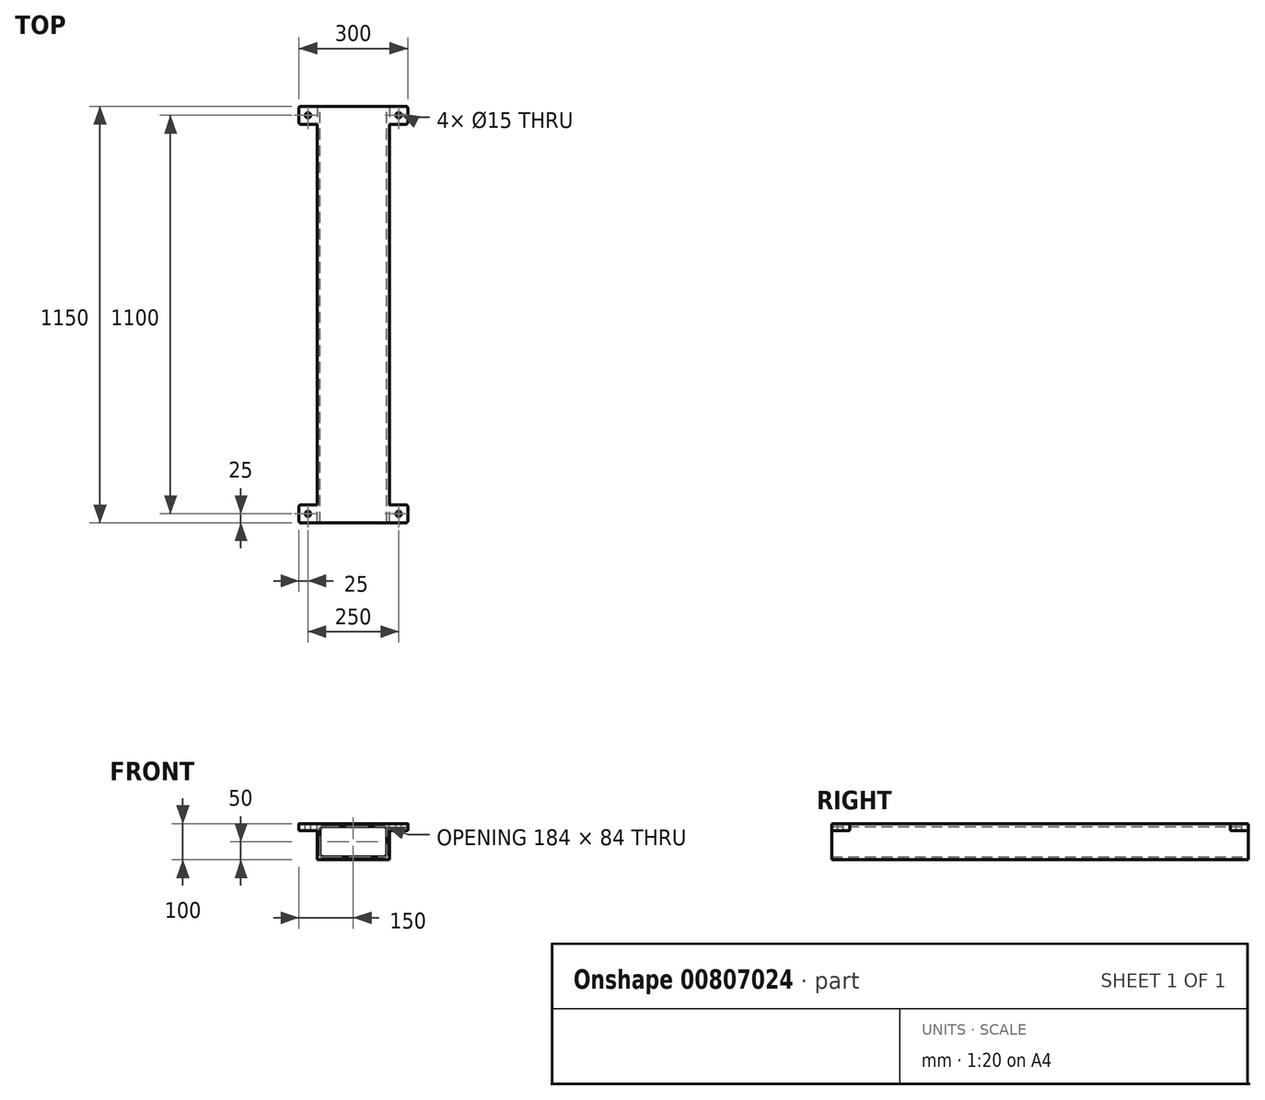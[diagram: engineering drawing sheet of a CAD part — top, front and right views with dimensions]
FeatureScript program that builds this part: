
annotation { "Feature Type Name" : "Feature", "Feature Type Description" : "" }
export const myFeature = defineFeature(function(context is Context, id is Id, definition is map)
    precondition{}
    {
        {
            var Q0;
            Q0=qCreatedBy(makeId("Front.planeOp"),FACE);
            var sketch = newSketch(context, id + "F0", { "sketchPlane" : qUnion([Q0])});
            skLineSegment(sketch, "E0.bottom", {"start": v(-100, 0) * mm, "end": v(100, 0) * mm});
            skLineSegment(sketch, "E0.top", {"start": v(-100, -100) * mm, "end": v(100, -100) * mm});
            skLineSegment(sketch, "E0.left", {"start": v(-100, 0) * mm, "end": v(-100, -100) * mm});
            skLineSegment(sketch, "E0.right", {"start": v(100, 0) * mm, "end": v(100, -100) * mm});
            skLineSegment(sketch, "E1.bottom", {"start": v(-82, -8) * mm, "end": v(82, -8) * mm});
            skLineSegment(sketch, "E1.top", {"start": v(-82, -92) * mm, "end": v(82, -92) * mm});
            skLineSegment(sketch, "E1.left", {"start": v(-92, -18) * mm, "end": v(-92, -82) * mm});
            skLineSegment(sketch, "E1.right", {"start": v(92, -18) * mm, "end": v(92, -82) * mm});
            skPoint(sketch, "E2.visualSharp", {"position": v(-92, -8) * mm});
            skArc(sketch, "E2.filletArc", {"start": v(-82, -8) * mm, "mid": v(-89.07, -10.93) * mm, "end": v(-92, -18) * mm});
            skPoint(sketch, "E3.visualSharp", {"position": v(92, -8) * mm});
            skArc(sketch, "E3.filletArc", {"start": v(92, -18) * mm, "mid": v(89.07, -10.93) * mm, "end": v(82, -8) * mm});
            skPoint(sketch, "E4.visualSharp", {"position": v(92, -92) * mm});
            skArc(sketch, "E4.filletArc", {"start": v(82, -92) * mm, "mid": v(89.07, -89.07) * mm, "end": v(92, -82) * mm});
            skPoint(sketch, "E5.visualSharp", {"position": v(-92, -92) * mm});
            skArc(sketch, "E5.filletArc", {"start": v(-92, -82) * mm, "mid": v(-89.07, -89.07) * mm, "end": v(-82, -92) * mm});
            skLineSegment(sketch, "E6", {"start": v(0, 0) * mm, "end": v(0, -112.71) * mm, "construction": true});
            skSolve(sketch);
        }
        {
            var Q0;
            Q0=makeQuery(id+"F0.imprint","IMPRINT",FACE,{"disambiguationData":[TD([[makeQuery(id+"F0.imprint","IMPRINT",EDGE,{"derivedFrom":sQuery(id+"F0.wireOp",EDGE,"E0.bottom")}),-1.0]])]});
            extrude(context, id + "F1", {"entities" : qUnion([Q0]), "endBound" : BoundingType.SYMMETRIC, "depth" : 1150 * mm, "offsetDistance" : 25 * mm});
        }
        {
            var Q0;
            Q0=makeQuery(id+"F1.opExtrude","SWEPT_FACE",FACE,{"disambiguationData":[OSD([sQuery(id+"F0.wireOp",EDGE,"E0.bottom")])]});
            var sketch = newSketch(context, id + "F2", { "sketchPlane" : qUnion([Q0])});
            skLineSegment(sketch, "E7.bottom", {"start": v(-100, -575) * mm, "end": v(-145, -575) * mm});
            skLineSegment(sketch, "E7.top", {"start": v(-100, -525) * mm, "end": v(-145, -525) * mm});
            skLineSegment(sketch, "E7.left", {"start": v(-100, -575) * mm, "end": v(-100, -525) * mm});
            skLineSegment(sketch, "E7.right", {"start": v(-150, -570) * mm, "end": v(-150, -530) * mm});
            skCircle(sketch, "E8", {"center": v(-125, -550) * mm, "radius": 7.5 * mm});
            skPoint(sketch, "E8.centerSnap0", {"position": v(-125, -525) * mm});
            skPoint(sketch, "E8.centerSnap1", {"position": v(-150, -550) * mm});
            skPoint(sketch, "E9.visualSharp", {"position": v(-150, -525) * mm});
            skArc(sketch, "E9.filletArc", {"start": v(-145, -525) * mm, "mid": v(-148.54, -526.46) * mm, "end": v(-150, -530) * mm});
            skPoint(sketch, "E10.visualSharp", {"position": v(-150, -575) * mm});
            skArc(sketch, "E10.filletArc", {"start": v(-150, -570) * mm, "mid": v(-148.54, -573.54) * mm, "end": v(-145, -575) * mm});
            skSolve(sketch);
        }
        {
            var Q0;
            Q0 = qSketchRegion(id + "F2", true);
            extrude(context, id + "F3", {"entities" : qUnion([Q0]), "oppositeDirection" : true, "depth" : 20 * mm, "offsetDistance" : 25 * mm});
        }
        {
            var Q0;
            Q0=makeQuery(id+"F3.opExtrude","SWEPT_BODY",BODY,{"disambiguationData":[OSD([sQuery(id+"F2.wireOp",EDGE,"E7.bottom"),sQuery(id+"F2.wireOp",EDGE,"E7.top"),sQuery(id+"F2.wireOp",EDGE,"E7.left"),sQuery(id+"F2.wireOp",EDGE,"E7.right"),sQuery(id+"F2.wireOp",EDGE,"E8"),sQuery(id+"F2.wireOp",EDGE,"E9.filletArc"),sQuery(id+"F2.wireOp",EDGE,"E10.filletArc")])]});
            var Q1;
            Q1=qCreatedBy(makeId("Front.planeOp"),FACE);
            mirror(context, id + "F4", {"entities" : qUnion([Q0]), "mirrorPlane" : qUnion([Q1])});
        }
        {
            var Q0;
            Q0=makeQuery(id+"F3.opExtrude","SWEPT_BODY",BODY,{"disambiguationData":[OSD([sQuery(id+"F2.wireOp",EDGE,"E7.bottom"),sQuery(id+"F2.wireOp",EDGE,"E7.top"),sQuery(id+"F2.wireOp",EDGE,"E7.left"),sQuery(id+"F2.wireOp",EDGE,"E7.right"),sQuery(id+"F2.wireOp",EDGE,"E8"),sQuery(id+"F2.wireOp",EDGE,"E9.filletArc"),sQuery(id+"F2.wireOp",EDGE,"E10.filletArc")])]});
            var Q1;
            Q1=makeQuery(id+"F4.opPattern","COPY",BODY,{"derivedFrom":makeQuery(id+"F3.opExtrude","SWEPT_BODY",BODY,{"disambiguationData":[OSD([sQuery(id+"F2.wireOp",EDGE,"E7.bottom"),sQuery(id+"F2.wireOp",EDGE,"E7.top"),sQuery(id+"F2.wireOp",EDGE,"E7.left"),sQuery(id+"F2.wireOp",EDGE,"E7.right"),sQuery(id+"F2.wireOp",EDGE,"E8"),sQuery(id+"F2.wireOp",EDGE,"E9.filletArc"),sQuery(id+"F2.wireOp",EDGE,"E10.filletArc")])]}),"instanceName":"1"});
            var Q2;
            Q2=qCreatedBy(makeId("Right.planeOp"),FACE);
            mirror(context, id + "F5", {"operationType" : NewBodyOperationType.ADD, "entities" : qUnion([Q0, Q1]), "mirrorPlane" : qUnion([Q2])});
        }
    });
